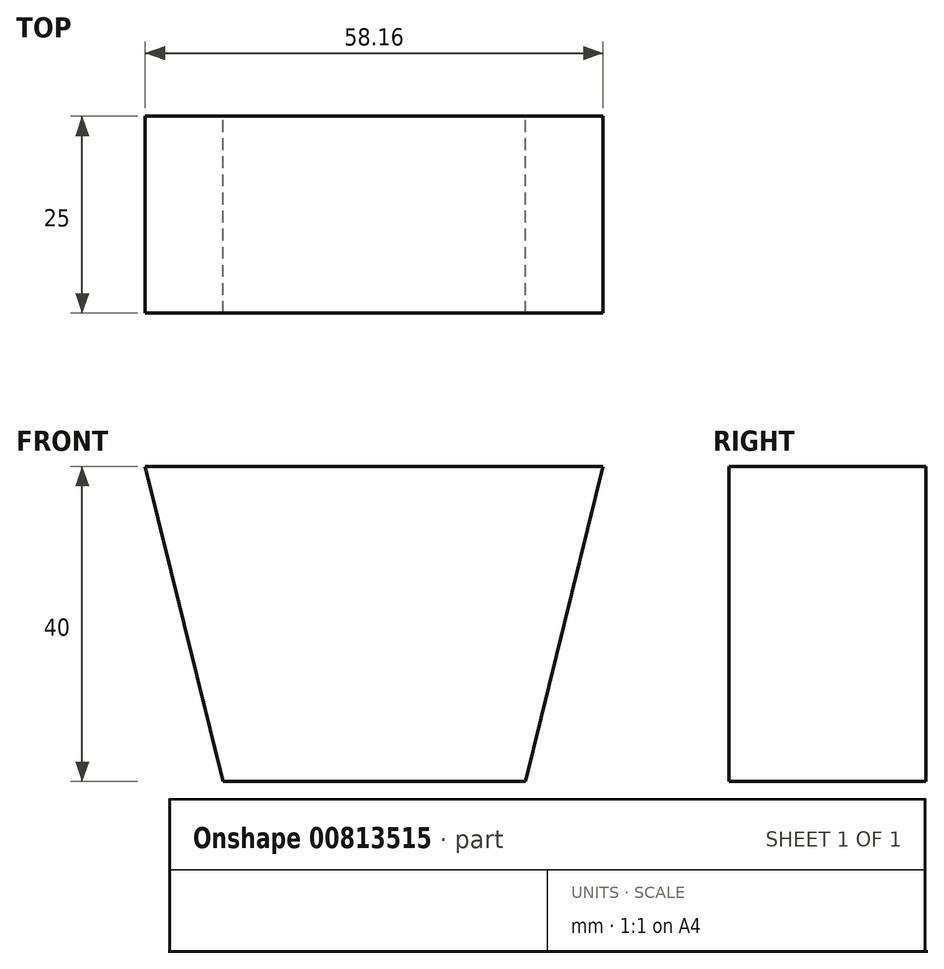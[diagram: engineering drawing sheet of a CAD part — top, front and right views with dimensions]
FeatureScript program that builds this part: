
annotation { "Feature Type Name" : "Feature", "Feature Type Description" : "" }
export const myFeature = defineFeature(function(context is Context, id is Id, definition is map)
    precondition{}
    {
        {
            var Q0;
            Q0=qCreatedBy(makeId("Front.planeOp"),FACE);
            var sketch = newSketch(context, id + "F0", { "sketchPlane" : qUnion([Q0])});
            skLineSegment(sketch, "E0", {"start": v(-29.08, 20) * mm, "end": v(29.08, 20) * mm});
            skLineSegment(sketch, "E1", {"start": v(29.08, 20) * mm, "end": v(19.22, -20) * mm});
            skLineSegment(sketch, "E2", {"start": v(19.22, -20) * mm, "end": v(-19.22, -20) * mm});
            skLineSegment(sketch, "E3", {"start": v(-19.22, -20) * mm, "end": v(-29.08, 20) * mm});
            skSolve(sketch);
        }
        {
            var Q0;
            Q0=makeQuery(id+"F0.imprint","IMPRINT",FACE,{"disambiguationData":[TD([[makeQuery(id+"F0.imprint","IMPRINT",EDGE,{"derivedFrom":sQuery(id+"F0.wireOp",EDGE,"E0")}),-1.0]])]});
            extrude(context, id + "F1", {"entities" : qUnion([Q0]), "depth" : 25 * mm, "offsetDistance" : 25 * mm});
        }
    });
